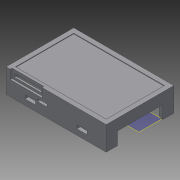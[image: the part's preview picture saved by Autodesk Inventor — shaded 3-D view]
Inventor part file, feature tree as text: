
AUTODESK INVENTOR PART (.ipt)
format: ipt  version: 2014 (Build 180170000, 170)  size: 280,064 bytes
history: native  units: mm
features: reference x16, sketch x12, extrude x10, other x4, projected_geometry x2, fillet x1, chamfer x1
ambient origin geometry x8: Origin, YZ Plane, XZ Plane, XY Plane, X Axis, Y Axis, Z Axis, Center Point
bodies: Volumenkörper1 (feature_tree)
feature tree (46):
  other  "Boden"
  other  "EbeneBoden"
  other  "EbeneWändeEnde"
  sketch  "SkizzeWände"  dims[d11=20.0mm d12=1.5mm]
  extrude  "Wände"  Depth=1.5mm TaperAngle=0.0deg
  sketch  "SkizzeAuflage"  dims[d13=4.0mm]
  other  "EbeneAuflage"
  extrude  "Auflage"  Depth=1.5mm TaperAngle=0.0deg
  extrude  "SDHilfe"  Depth=1.5mm
  extrude  "LED"  Depth=2.0mm
  fillet  "RundungLED"  Radius=10.0mm
  extrude  "USB"  Depth=1.5mm
  chamfer  "FaseUSB"  [1 undecoded]
  extrude  "JSTFC"  Depth=0.3mm
  extrude  "JSTOSD"  Depth=1.0mm
  extrude  "Lippe"  Depth=0.8mm TaperAngle=0.0deg
  extrude  "Schnapper"  Depth=0.8mm TaperAngle=0.0deg
  extrude  "Aufkleber"  Depth=0.3mm
  sketch  "SkizzeBoden"  dims[d14=2.0mm d15=0.0mm d16=0.0mm]
  reference  "Referenz1"
  projected_geometry  "Projizierte Kontur1"
  sketch  "SkizzeSD"  dims[d17=0.3mm d18=0.3mm]
  reference  "Referenz5"
  sketch  "Skizze7"  dims[d0=1.6mm d1=1.5mm d2=0.0mm]
  sketch  "SkizzeLED"  dims[d19=1.5mm d20=0.0mm d21=1.0mm]
  reference  "Referenz6"
  reference  "Referenz7"
  reference  "Referenz8"
  reference  "Referenz9"
  sketch  "SkizzeUSB"  dims[d22=1.0mm d23=0.8mm d24=0.0mm]
  reference  "Referenz10"
  reference  "Referenz11"
  sketch  "Skizze10"  dims[d3=1.5mm d4=1.5mm d5=0.0mm]
  reference  "Referenz12"
  reference  "Referenz13"
  sketch  "Skizze11"  dims[d6=5.0mm d7=1.5mm]
  reference  "Referenz14"
  reference  "Referenz15"
  sketch  "Skizze12"  dims[d8=8.0mm d9=2.0mm d10=10.0mm]
  sketch  "SkizzeSchnapper"  dims[d25=0.1mm d27=0.8mm d28=0.0mm]
  reference  "Referenz16"
  reference  "Referenz17"
  reference  "Referenz18"
  projected_geometry  "Projizierte Kontur4"
  reference  "Referenz19"
  sketch  "SkizzeAufkleber"  dims[d29=0.3mm d30=0.3mm d31=0.8mm d32=0.0mm d33=1.5mm d34=2.0mm d35=45.0deg d36=0.3mm d38=0.3mm d39=0.8mm d40=0.0mm d41=0.3mm d42=0.3mm d43=0.8mm d44=0.0mm d45=0.8mm d46=0.8mm d47=0.6mm d48=0.0mm d49=4.5mm d50=1.8mm d51=1.2mm d52=1.6mm d53=1.2mm d54=0.8mm d55=0.0mm d56=2.0mm d57=2.0mm d58=0.3mm d59=0.0mm d60=0.3mm]
note: 1 required parameter value undecoded (feature->parameter linkage not recoverable at this tier; creation-order binding heuristic only, values carry confidence <= 0.55)
